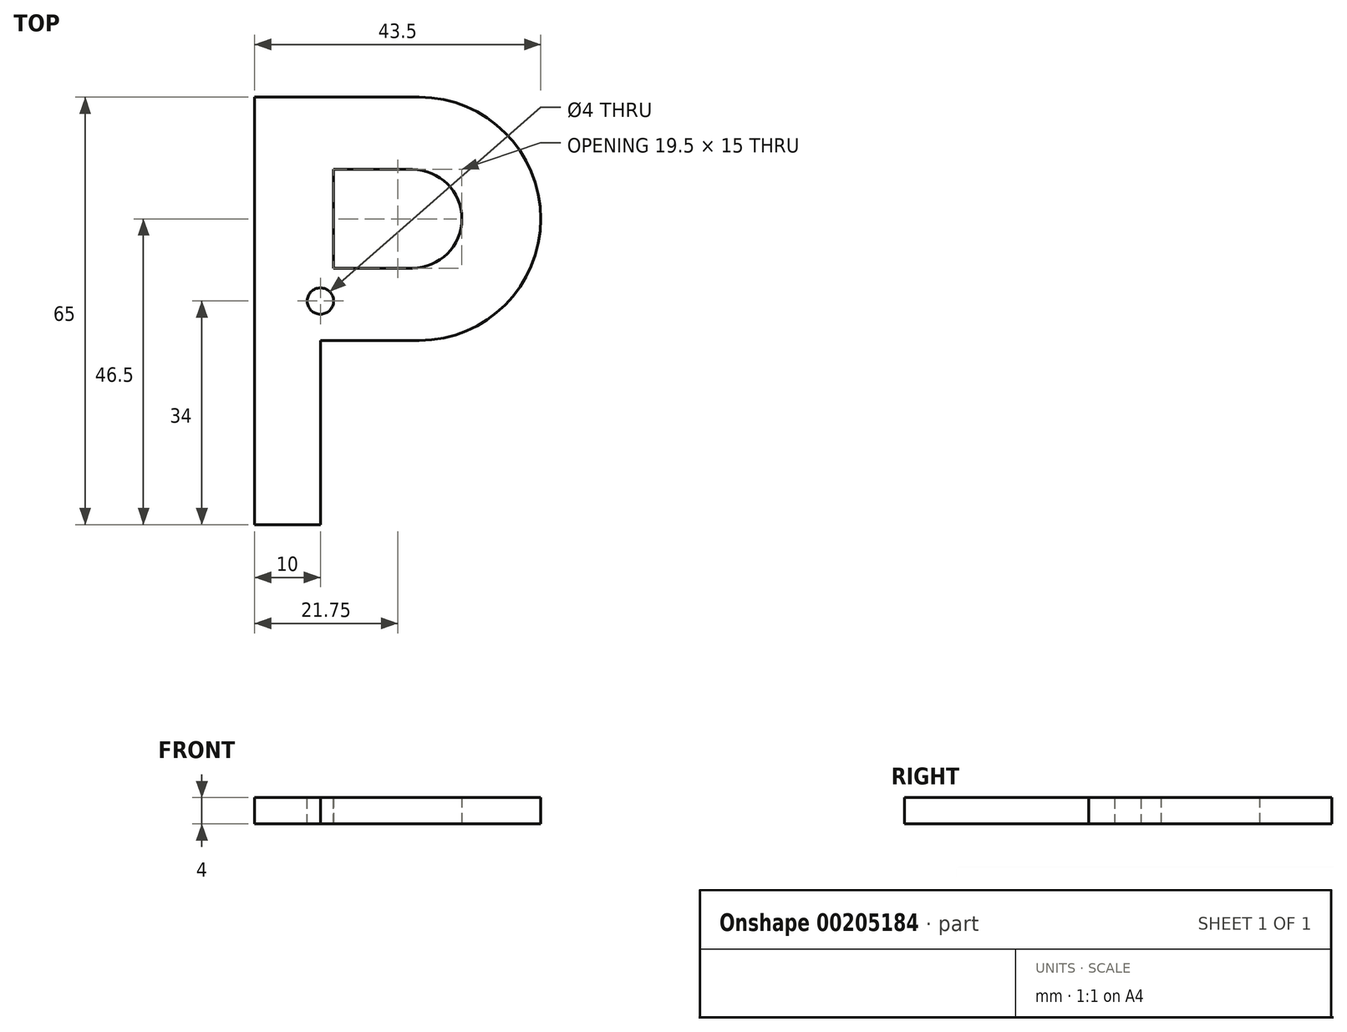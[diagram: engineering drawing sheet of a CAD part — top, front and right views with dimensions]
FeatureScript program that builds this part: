
annotation { "Feature Type Name" : "Feature", "Feature Type Description" : "" }
export const myFeature = defineFeature(function(context is Context, id is Id, definition is map)
    precondition{}
    {
        {
            var Q0;
            Q0=qCreatedBy(makeId("Top.planeOp"),FACE);
            var sketch = newSketch(context, id + "F0", { "sketchPlane" : qUnion([Q0])});
            skLineSegment(sketch, "E0", {"start": v(-30, 32.5) * mm, "end": v(-30, -32.5) * mm});
            skLineSegment(sketch, "E1", {"start": v(-30, 32.5) * mm, "end": v(-5, 32.5) * mm});
            skLineSegment(sketch, "E2", {"start": v(-5, 32.5) * mm, "end": v(-5, -4.5) * mm, "construction": true});
            skArc(sketch, "E3", {"start": v(-5, -4.5) * mm, "mid": v(13.5, 14) * mm, "end": v(-5, 32.5) * mm});
            skLineSegment(sketch, "E4", {"start": v(-30, -32.5) * mm, "end": v(-20, -32.5) * mm});
            skLineSegment(sketch, "E5", {"start": v(-20, -32.5) * mm, "end": v(-20, -4.5) * mm});
            skLineSegment(sketch, "E6", {"start": v(-20, -4.5) * mm, "end": v(-5, -4.5) * mm});
            skLineSegment(sketch, "E7.bottom", {"start": v(-18, 21.5) * mm, "end": v(-6, 21.5) * mm});
            skLineSegment(sketch, "E7.top", {"start": v(-18, 6.5) * mm, "end": v(-6, 6.5) * mm});
            skLineSegment(sketch, "E7.left", {"start": v(-18, 21.5) * mm, "end": v(-18, 6.5) * mm});
            skLineSegment(sketch, "E7.right", {"start": v(-6, 21.5) * mm, "end": v(-6, 6.5) * mm, "construction": true});
            skArc(sketch, "E8", {"start": v(-6, 6.5) * mm, "mid": v(1.5, 14) * mm, "end": v(-6, 21.5) * mm});
            skSolve(sketch);
        }
        {
            var Q0;
            Q0=makeQuery(id+"F0.imprint","IMPRINT",FACE,{"disambiguationData":[TD([[makeQuery(id+"F0.imprint","IMPRINT",EDGE,{"derivedFrom":sQuery(id+"F0.wireOp",EDGE,"E0")}),1.0]])]});
            var Q1;
            Q1=sQuery(id+"F0.wireOp",EDGE,"E7.right");
            extrude(context, id + "F1", {"entities" : qUnion([Q0]), "surfaceEntities" : qUnion([Q1]), "depth" : 4 * mm});
        }
        {
            var Q0;
            Q0=makeQuery(id+"F1.opExtrude","CAP_FACE",FACE,{"disambiguationData":[OSD([sQuery(id+"F0.wireOp",EDGE,"E0"),sQuery(id+"F0.wireOp",EDGE,"E1"),sQuery(id+"F0.wireOp",EDGE,"E3"),sQuery(id+"F0.wireOp",EDGE,"E4"),sQuery(id+"F0.wireOp",EDGE,"E5"),sQuery(id+"F0.wireOp",EDGE,"06ESDlr4-8qJE-ybJR-heob-LvEuj66mLRZU"),sQuery(id+"F0.wireOp",EDGE,"E6"),sQuery(id+"F0.wireOp",EDGE,"kiPQuws6-YIgo-x2S1-cFug-ELzqnbIVYZ47"),sQuery(id+"F0.wireOp",EDGE,"WRBl6du7-ib8s-VOXu-fA5x-PmYFZVqNdRJz"),sQuery(id+"F0.wireOp",EDGE,"E7.bottom"),sQuery(id+"F0.wireOp",EDGE,"E7.top"),sQuery(id+"F0.wireOp",EDGE,"E7.left"),sQuery(id+"F0.wireOp",EDGE,"E8")])],"isStart":false});
            var sketch = newSketch(context, id + "F2", { "sketchPlane" : qUnion([Q0])});
            skCircle(sketch, "E9", {"center": v(-20, 1.5) * mm, "radius": 2 * mm});
            skSolve(sketch);
        }
        {
            var Q0;
            Q0=qSketchRegion(id+"F2",true);
            extrude(context, id + "F3", {"entities" : qUnion([Q0]), "operationType" : NewBodyOperationType.REMOVE, "endBound" : BoundingType.THROUGH_ALL, "oppositeDirection" : true, "depth" : 25 * mm});
        }
    });
